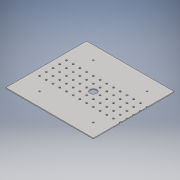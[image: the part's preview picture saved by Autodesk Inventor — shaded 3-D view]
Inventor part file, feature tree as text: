
AUTODESK INVENTOR PART (.ipt)
format: ipt  version: 2018 (Build 220112000, 112)  size: 237,568 bytes
history: native  units: in
note: dims shown in document units (in); Inventor stores cm internally (conversion verified against a paired STEP export)
features: extrude x5, sketch x4
ambient origin geometry x8: Origin, YZ Plane, XZ Plane, XY Plane, X Axis, Y Axis, Z Axis, Center Point
bodies: Solid1 (feature_tree)
feature tree (9):
  extrude  "Extrusion1"  Depth=0.125in
  extrude  "Extrusion2"  Depth=2.0in TaperAngle=0.0deg
  extrude  "Extrusion3"  Depth=0.25in
  extrude  "Extrusion4"  Depth=12.0in
  extrude  "Extrusion6"  Depth=12.0in TaperAngle=0.0deg
  sketch  "Sketch1"  dims[d2=0.125in d3=0.0in d4=6.0in]
  sketch  "Sketch2"  dims[d5=1.0in d6=2.0in d7=0.0in]
  sketch  "Sketch3"  dims[d9=0.25in d11=0.25in]
  sketch  "Sketch4"  dims[d12=0.25in d13=0.25in d14=0.25in d15=0.25in d18=0.25in d19=0.25in d20=0.25in d21=0.25in d22=0.25in d23=0.25in d24=0.25in d25=0.25in d26=0.25in d27=0.25in d28=0.25in d29=0.25in d33=0.25in d35=0.25in d36=0.25in d37=0.25in d38=0.25in d39=0.25in d41=0.25in d43=0.25in d44=0.25in d45=0.25in d46=0.25in d47=0.25in d48=2.0in d49=0.0in d54=1.0in d55=1.0in d56=0.25in d57=0.25in d59=2.0in d60=0.0in d63=0.2031in d67=8.0in d69=0.2031in d70=0.2031in d73=13.0in d74=13.0in d75=12.0in d76=0.2031in d77=1.0in d78=0.0in]
